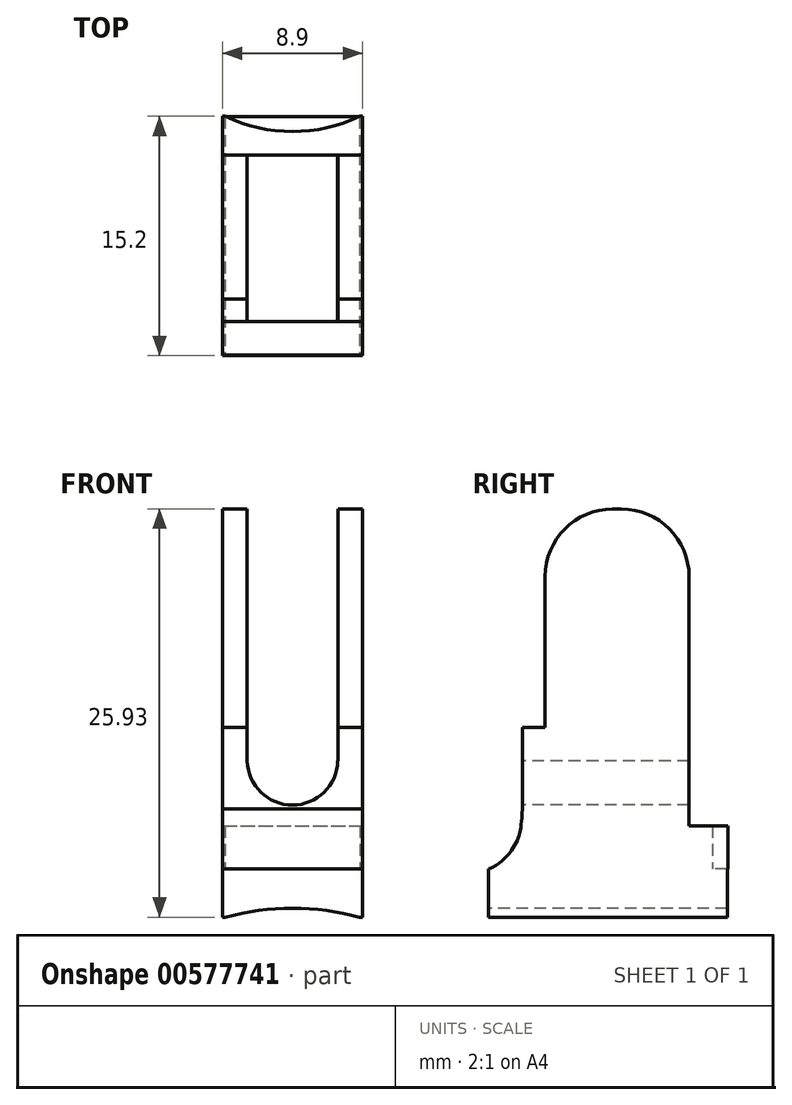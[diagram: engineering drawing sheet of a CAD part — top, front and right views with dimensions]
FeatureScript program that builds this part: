
annotation { "Feature Type Name" : "Feature", "Feature Type Description" : "" }
export const myFeature = defineFeature(function(context is Context, id is Id, definition is map)
    precondition{}
    {
        {
            var Q0;
            Q0=qCreatedBy(makeId("Top.planeOp"),FACE);
            var sketch = newSketch(context, id + "F0", { "sketchPlane" : qUnion([Q0])});
            skLineSegment(sketch, "E0.bottom", {"start": v(-4.44, 7.62) * mm, "end": v(4.45, 7.62) * mm});
            skLineSegment(sketch, "E0.top", {"start": v(-4.45, -7.62) * mm, "end": v(4.44, -7.62) * mm});
            skLineSegment(sketch, "E0.left", {"start": v(-4.44, 7.62) * mm, "end": v(-4.45, -7.62) * mm});
            skLineSegment(sketch, "E0.right", {"start": v(4.45, 7.62) * mm, "end": v(4.44, -7.62) * mm});
            skPoint(sketch, "E0.middle", {"position": v(0, 0) * mm});
            skSolve(sketch);
        }
        {
            var Q0;
            Q0 = qSketchRegion(id + "F0", true);
            extrude(context, id + "F1", {"entities" : qUnion([Q0]), "depth" : 22.86 * mm, "offsetDistance" : 25.4 * mm});
        }
        {
            var Q0;
            Q0=qCreatedBy(makeId("Right.planeOp"),FACE);
            var sketch = newSketch(context, id + "F2", { "sketchPlane" : qUnion([Q0])});
            skLineSegment(sketch, "E1", {"start": v(7.84, 0) * mm, "end": v(7.84, 2.73) * mm});
            skLineSegment(sketch, "E2", {"start": v(7.84, 2.73) * mm, "end": v(5.16, 2.73) * mm});
            skLineSegment(sketch, "E3", {"start": v(5.16, 2.73) * mm, "end": v(5.16, 24.55) * mm});
            skLineSegment(sketch, "E4", {"start": v(5.16, 24.55) * mm, "end": v(12.5, 24.55) * mm});
            skLineSegment(sketch, "E5", {"start": v(12.5, 24.55) * mm, "end": v(12.5, 0) * mm});
            skLineSegment(sketch, "E6", {"start": v(12.5, 0) * mm, "end": v(7.84, 0) * mm});
            skSolve(sketch);
        }
        {
            var Q0;
            Q0=makeQuery(id+"F2.imprint","IMPRINT",FACE,{"disambiguationData":[TD([[makeQuery(id+"F2.imprint","IMPRINT",EDGE,{"derivedFrom":sQuery(id+"F2.wireOp",EDGE,"E1")}),-1.0]])]});
            extrude(context, id + "F3", {"entities" : qUnion([Q0]), "operationType" : NewBodyOperationType.REMOVE, "oppositeDirection" : true, "depth" : 25.4 * mm, "offsetDistance" : 25.4 * mm, "hasSecondDirection" : true, "secondDirectionOppositeDirection" : false, "secondDirectionDepth" : 25.4 * mm});
        }
        {
            var Q0;
            Q0=makeQuery(id+"F3.boolean.opBoolean","INTERSECT",EDGE,{"derivedFrom":[makeQuery(id+"F1.opExtrude","CAP_FACE",FACE,{"disambiguationData":[OSD([sQuery(id+"F0.wireOp",EDGE,"E0.bottom"),sQuery(id+"F0.wireOp",EDGE,"E0.top"),sQuery(id+"F0.wireOp",EDGE,"E0.left"),sQuery(id+"F0.wireOp",EDGE,"E0.right")])],"isStart":false}),makeQuery(id+"F3.opExtrude","SWEPT_FACE",FACE,{"disambiguationData":[OSD([sQuery(id+"F2.wireOp",EDGE,"E3")])]})]});
            fillet(context, id + "F4", {"entities" : qUnion([Q0]), "radius" : 4.3 * mm, "tangentPropagation" : true, "allowEdgeOverflow" : false});
        }
        {
            var Q0;
            Q0=qCreatedBy(makeId("Right.planeOp"),FACE);
            var sketch = newSketch(context, id + "F5", { "sketchPlane" : qUnion([Q0])});
            skLineSegment(sketch, "E7", {"start": v(-9.26, 8.98) * mm, "end": v(-3.99, 8.98) * mm});
            skLineSegment(sketch, "E8", {"start": v(-3.99, 8.98) * mm, "end": v(-3.99, 24.72) * mm});
            skLineSegment(sketch, "E9", {"start": v(-3.99, 24.72) * mm, "end": v(-11.59, 24.72) * mm});
            skLineSegment(sketch, "E10", {"start": v(-11.59, 24.72) * mm, "end": v(-11.59, 8.98) * mm});
            skLineSegment(sketch, "E11", {"start": v(-11.59, 8.98) * mm, "end": v(-9.26, 8.98) * mm});
            skSolve(sketch);
        }
        {
            var Q0;
            Q0=makeQuery(id+"F5.imprint","IMPRINT",FACE,{"disambiguationData":[TD([[makeQuery(id+"F5.imprint","IMPRINT",EDGE,{"derivedFrom":sQuery(id+"F5.wireOp",EDGE,"E7")}),1.0]])]});
            extrude(context, id + "F6", {"entities" : qUnion([Q0]), "operationType" : NewBodyOperationType.REMOVE, "oppositeDirection" : true, "depth" : 25.4 * mm, "offsetDistance" : 25.4 * mm, "hasSecondDirection" : true, "secondDirectionOppositeDirection" : false, "secondDirectionDepth" : 25.4 * mm});
        }
        {
            var Q0;
            Q0=makeQuery(id+"F6.boolean.opBoolean","INTERSECT",EDGE,{"derivedFrom":[makeQuery(id+"F1.opExtrude","CAP_FACE",FACE,{"disambiguationData":[OSD([sQuery(id+"F0.wireOp",EDGE,"E0.bottom"),sQuery(id+"F0.wireOp",EDGE,"E0.top"),sQuery(id+"F0.wireOp",EDGE,"E0.left"),sQuery(id+"F0.wireOp",EDGE,"E0.right")])],"isStart":false}),makeQuery(id+"F6.opExtrude","SWEPT_FACE",FACE,{"disambiguationData":[OSD([sQuery(id+"F5.wireOp",EDGE,"E8")])]})]});
            fillet(context, id + "F7", {"entities" : qUnion([Q0]), "radius" : 4.3 * mm, "tangentPropagation" : true, "allowEdgeOverflow" : false});
        }
        {
            var Q0;
            Q0=qCreatedBy(makeId("Right.planeOp"),FACE);
            var sketch = newSketch(context, id + "F8", { "sketchPlane" : qUnion([Q0])});
            skLineSegment(sketch, "E12", {"start": v(-5.42, 10.04) * mm, "end": v(-5.42, 3.82) * mm});
            skFitSpline(sketch, "E13", {"points": [v(-5.42, 3.82) * mm, v(-5.74, 1.85) * mm, v(-7.54, 0) * mm, v(-13.45, 0.47) * mm], "startDerivative": vector(-1.23, -13.56) * mm, "endDerivative": vector(-15.24, 3.33) * mm});
            skLineSegment(sketch, "E14", {"start": v(-13.45, 0.47) * mm, "end": v(-13.45, 9.93) * mm});
            skLineSegment(sketch, "E15", {"start": v(-13.45, 9.93) * mm, "end": v(-5.42, 10.04) * mm});
            skSolve(sketch);
        }
        {
            var Q0;
            Q0=makeQuery(id+"F8.imprint","IMPRINT",FACE,{"disambiguationData":[TD([[makeQuery(id+"F8.imprint","IMPRINT",EDGE,{"derivedFrom":sQuery(id+"F8.wireOp",EDGE,"E12")}),-1.0]])]});
            extrude(context, id + "F9", {"entities" : qUnion([Q0]), "operationType" : NewBodyOperationType.REMOVE, "oppositeDirection" : true, "depth" : 25.4 * mm, "offsetDistance" : 25.4 * mm, "hasSecondDirection" : true, "secondDirectionOppositeDirection" : false, "secondDirectionDepth" : 25.4 * mm});
        }
        {
            var Q0;
            Q0=qCreatedBy(makeId("Top.planeOp"),FACE);
            var sketch = newSketch(context, id + "F10", { "sketchPlane" : qUnion([Q0])});
            skCircle(sketch, "E16", {"center": v(0, 16.54) * mm, "radius": 9.9 * mm});
            skSolve(sketch);
        }
        {
            var Q0;
            Q0=makeQuery(id+"F10.imprint","IMPRINT",FACE,{"disambiguationData":[TD([[makeQuery(id+"F10.imprint","IMPRINT",EDGE,{"derivedFrom":sQuery(id+"F10.wireOp",EDGE,"E16")}),1.0]])]});
            extrude(context, id + "F11", {"entities" : qUnion([Q0]), "operationType" : NewBodyOperationType.REMOVE, "depth" : 48.5 * mm, "offsetDistance" : 25.4 * mm});
        }
        {
            var Q0;
            Q0=qCreatedBy(makeId("Front.planeOp"),FACE);
            var sketch = newSketch(context, id + "F12", { "sketchPlane" : qUnion([Q0])});
            skCircle(sketch, "E17", {"center": v(0, 6.93) * mm, "radius": 2.88 * mm});
            skSolve(sketch);
        }
        {
            var Q0;
            Q0 = qSketchRegion(id + "F12", true);
            extrude(context, id + "F13", {"entities" : qUnion([Q0]), "operationType" : NewBodyOperationType.REMOVE, "oppositeDirection" : true, "depth" : 25.4 * mm, "offsetDistance" : 25.4 * mm, "hasSecondDirection" : true, "secondDirectionOppositeDirection" : false, "secondDirectionDepth" : 25.4 * mm});
        }
        {
            var Q0;
            Q0=qCreatedBy(makeId("Front.planeOp"),FACE);
            var sketch = newSketch(context, id + "F14", { "sketchPlane" : qUnion([Q0])});
            skLineSegment(sketch, "E18", {"start": v(2.88, 6.86) * mm, "end": v(2.88, 24.08) * mm});
            skLineSegment(sketch, "E19", {"start": v(2.88, 24.08) * mm, "end": v(-1.05, 24.08) * mm});
            skLineSegment(sketch, "E20", {"start": v(-1.05, 24.08) * mm, "end": v(0, 23.82) * mm});
            skLineSegment(sketch, "E21", {"start": v(0, 23.82) * mm, "end": v(0, 6.86) * mm});
            skLineSegment(sketch, "E22", {"start": v(0, 6.86) * mm, "end": v(2.88, 6.86) * mm});
            skLineSegment(sketch, "E23", {"start": v(0, 6.86) * mm, "end": v(-2.88, 6.86) * mm});
            skLineSegment(sketch, "E24", {"start": v(-2.88, 6.86) * mm, "end": v(-2.88, 24.2) * mm});
            skLineSegment(sketch, "E25", {"start": v(-2.88, 24.2) * mm, "end": v(0, 23.82) * mm});
            skSolve(sketch);
        }
        {
            var Q0;
            Q0=makeQuery(id+"F14.imprint","IMPRINT",FACE,{"disambiguationData":[TD([[makeQuery(id+"F14.imprint","IMPRINT",EDGE,{"derivedFrom":sQuery(id+"F14.wireOp",EDGE,"E21")}),-1.0]])]});
            var Q1;
            Q1=makeQuery(id+"F14.imprint","IMPRINT",FACE,{"disambiguationData":[TD([[makeQuery(id+"F14.imprint","IMPRINT",EDGE,{"derivedFrom":sQuery(id+"F14.wireOp",EDGE,"E18")}),1.0]])]});
            extrude(context, id + "F15", {"entities" : qUnion([Q0, Q1]), "operationType" : NewBodyOperationType.REMOVE, "oppositeDirection" : true, "depth" : 25.4 * mm, "offsetDistance" : 25.4 * mm, "hasSecondDirection" : true, "secondDirectionOppositeDirection" : false, "secondDirectionDepth" : 25.4 * mm});
        }
        {
            var Q0;
            Q0=qCreatedBy(makeId("Top.planeOp"),FACE);
            var sketch = newSketch(context, id + "F16", { "sketchPlane" : qUnion([Q0])});
            skLineSegment(sketch, "E26.bottom", {"start": v(-4.44, -7.58) * mm, "end": v(4.45, -7.58) * mm});
            skLineSegment(sketch, "E26.top", {"start": v(-4.45, 7.58) * mm, "end": v(4.44, 7.58) * mm});
            skLineSegment(sketch, "E26.left", {"start": v(-4.44, -7.58) * mm, "end": v(-4.45, 7.58) * mm});
            skLineSegment(sketch, "E26.right", {"start": v(4.45, -7.58) * mm, "end": v(4.44, 7.58) * mm});
            skPoint(sketch, "E26.middle", {"position": v(0, 0) * mm});
            skSolve(sketch);
        }
        {
            var Q0;
            Q0=makeQuery(id+"F16.imprint","IMPRINT",FACE,{"disambiguationData":[TD([[makeQuery(id+"F16.imprint","IMPRINT",EDGE,{"derivedFrom":sQuery(id+"F16.wireOp",EDGE,"E26.bottom")}),1.0]])]});
            extrude(context, id + "F17", {"entities" : qUnion([Q0]), "operationType" : NewBodyOperationType.ADD, "oppositeDirection" : true, "depth" : 3.07 * mm, "offsetDistance" : 25.4 * mm});
        }
        {
            var Q0;
            Q0=qCreatedBy(makeId("Front.planeOp"),FACE);
            var sketch = newSketch(context, id + "F18", { "sketchPlane" : qUnion([Q0])});
            skCircle(sketch, "E27", {"center": v(0, -18.57) * mm, "radius": 16.08 * mm});
            skSolve(sketch);
        }
        {
            var Q0;
            Q0=makeQuery(id+"F18.imprint","IMPRINT",FACE,{"disambiguationData":[TD([[makeQuery(id+"F18.imprint","IMPRINT",EDGE,{"derivedFrom":sQuery(id+"F18.wireOp",EDGE,"E27")}),1.0]])]});
            extrude(context, id + "F19", {"entities" : qUnion([Q0]), "operationType" : NewBodyOperationType.REMOVE, "oppositeDirection" : true, "depth" : 25.4 * mm, "offsetDistance" : 25.4 * mm, "hasSecondDirection" : true, "secondDirectionOppositeDirection" : false, "secondDirectionDepth" : 25.4 * mm});
        }
    });
